# Revit family: Furniture-Medicine_Cabinet-KOHLER-Catalan-K-2943_1
name_source: partatom
category: Specialty Equipment
revit_build: Autodesk Revit 2017 (Build: 20160225_1515(x64)
units: mm (PartAtom-declared; Revit-internal decimal feet)

## family parameters
Cut with Voids When Loaded = No
Host = Face
OmniClass Number = 23.25.53.11.13.11
Part Type = Normal
Room Calculation Point = No
Round Connector Dimension = Use Diameter
Shared = No

## types (1)
- SAA-Satin Anodized Aluminum
    ADA Compliant = No
    Assembly Code = E20
    Date Modified = 08/14/2020
    Default Elevation = 60"
    Description = 24-1/8 inch W x 36-1/8 inch H aluminum single-door medicine cabinet with 170 degree hinge
    Finish = KOHLER-Metal-SAA-Satin_Anodized_Aluminum
    Height = 36 1/8"
    Length = 4 3/4"
    Manufacturer = KOHLER Co.
    Master Format 2014 = 06 41 93
    Master Format 2014 Name = Cabinet and Drawer Hardware
    Material = Anodized Aluminum
    Model = K-2943-PG-SAA
    Product Documentation Link = https://www.us.kohler.com
    Product Name = Catalan
    Product Page URL = http://www.us.kohler.com
    Type = 1
    URL = https://www.us.kohler.com
    WaterSense Certified = No
    Width = 24 1/8"

## geometry (parser evidence)
native form markers: Sweep x3
no freeform markers — native parametric forms only
